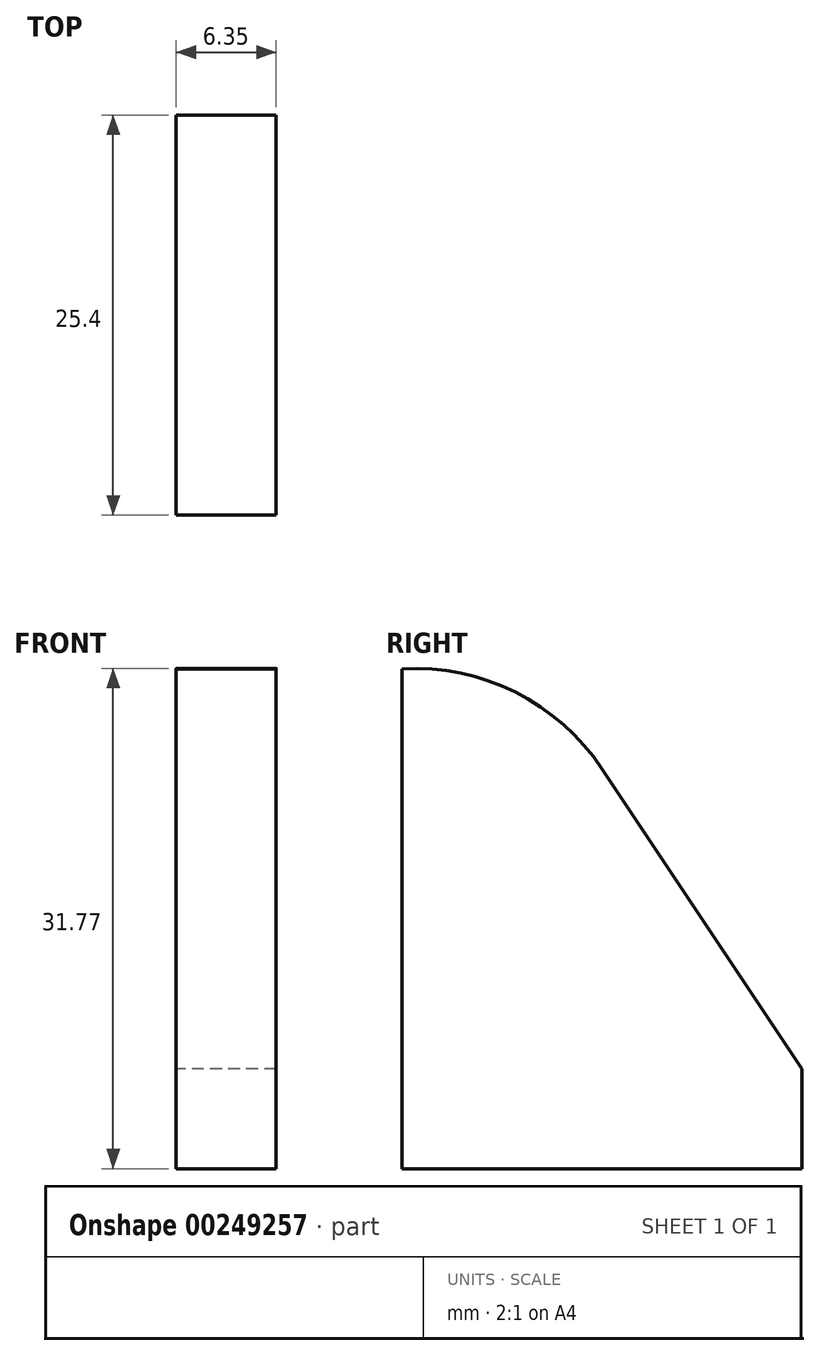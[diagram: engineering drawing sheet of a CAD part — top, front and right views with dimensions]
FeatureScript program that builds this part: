
annotation { "Feature Type Name" : "Feature", "Feature Type Description" : "" }
export const myFeature = defineFeature(function(context is Context, id is Id, definition is map)
    precondition{}
    {
        {
            var Q0;
            Q0=qCreatedBy(makeId("Right.planeOp"),FACE);
            var sketch = newSketch(context, id + "F0", { "sketchPlane" : qUnion([Q0])});
            skLineSegment(sketch, "E0", {"start": v(0, 0) * mm, "end": v(0, -31.75) * mm});
            skLineSegment(sketch, "E1", {"start": v(0, -31.75) * mm, "end": v(25.4, -31.75) * mm});
            skLineSegment(sketch, "E2", {"start": v(25.4, -31.75) * mm, "end": v(25.4, -25.4) * mm});
            skLineSegment(sketch, "E3", {"start": v(25.4, -25.4) * mm, "end": v(12.7, -6.35) * mm});
            skArc(sketch, "E4", {"start": v(12.7, -6.35) * mm, "mid": v(7.2, -1.49) * mm, "end": v(0, 0) * mm});
            skSolve(sketch);
        }
        {
            var Q0;
            Q0=makeQuery(id+"F0.imprint","IMPRINT",FACE,{"disambiguationData":[TD([[makeQuery(id+"F0.imprint","IMPRINT",EDGE,{"derivedFrom":sQuery(id+"F0.wireOp",EDGE,"E0")}),1.0]])]});
            extrude(context, id + "F1", {"entities" : qUnion([Q0]), "depth" : 6.35 * mm});
        }
    });
